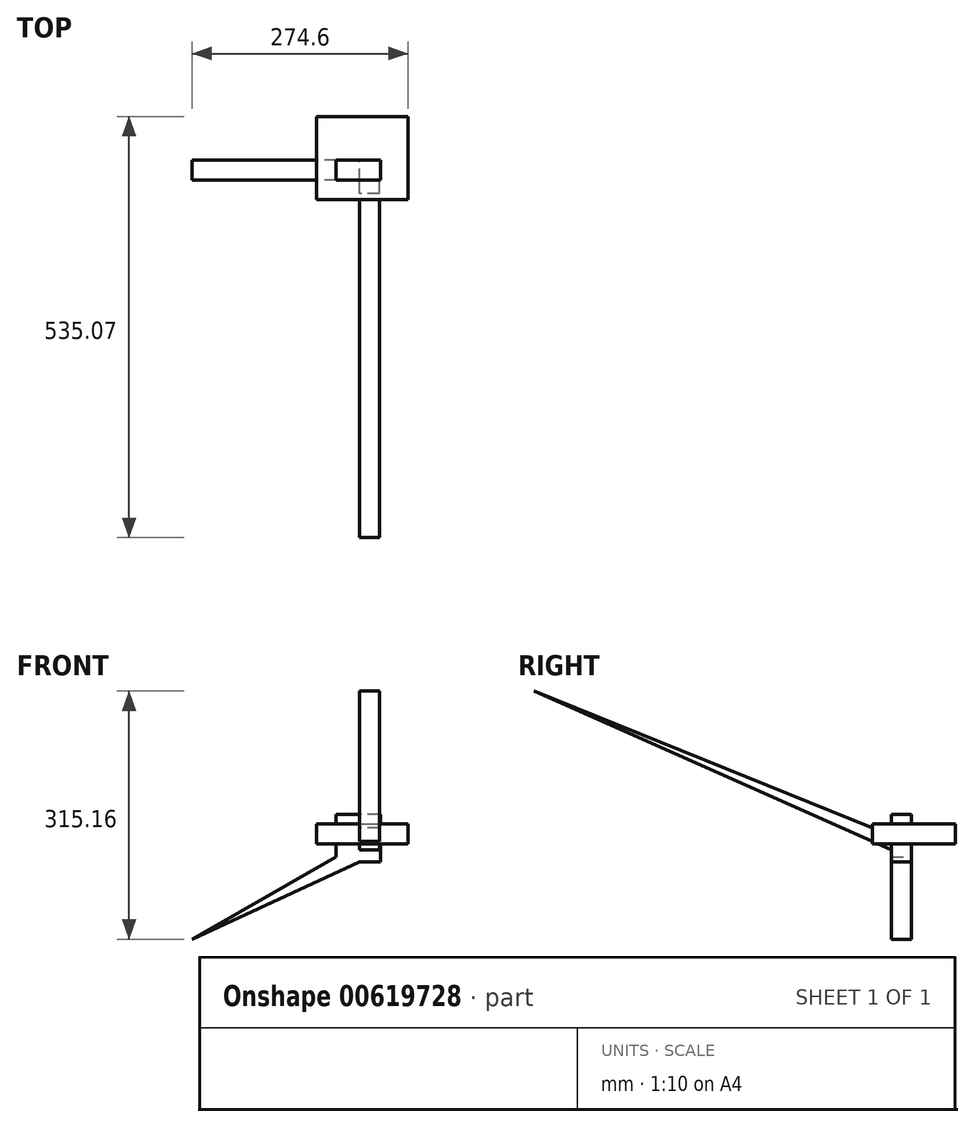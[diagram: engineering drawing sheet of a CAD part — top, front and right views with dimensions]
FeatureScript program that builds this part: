
annotation { "Feature Type Name" : "Feature", "Feature Type Description" : "" }
export const myFeature = defineFeature(function(context is Context, id is Id, definition is map)
    precondition{}
    {
        {
            var Q0;
            Q0=qCreatedBy(makeId("Top.planeOp"),FACE);
            var sketch = newSketch(context, id + "F0", { "sketchPlane" : qUnion([Q0])});
            skLineSegment(sketch, "E0.bottom", {"start": v(0, 0) * mm, "end": v(-54.42, 0) * mm});
            skLineSegment(sketch, "E0.top", {"start": v(0, 55.67) * mm, "end": v(-54.42, 55.67) * mm});
            skLineSegment(sketch, "E0.left", {"start": v(0, 0) * mm, "end": v(0, 55.67) * mm});
            skLineSegment(sketch, "E0.right", {"start": v(-54.42, 0) * mm, "end": v(-54.42, 55.67) * mm});
            skLineSegment(sketch, "E1.bottom", {"start": v(0, 0) * mm, "end": v(61.93, 0) * mm});
            skLineSegment(sketch, "E1.top", {"start": v(0, -49.98) * mm, "end": v(61.93, -49.98) * mm});
            skLineSegment(sketch, "E1.left", {"start": v(0, 0) * mm, "end": v(0, -49.98) * mm});
            skLineSegment(sketch, "E1.right", {"start": v(61.93, 0) * mm, "end": v(61.93, -49.98) * mm});
            skLineSegment(sketch, "E2.top", {"start": v(0, -49.98) * mm, "end": v(-54.42, -49.98) * mm});
            skLineSegment(sketch, "E2.right", {"start": v(-54.42, 0) * mm, "end": v(-54.42, -49.98) * mm});
            skLineSegment(sketch, "E3.top", {"start": v(0, 55.67) * mm, "end": v(61.93, 55.67) * mm});
            skLineSegment(sketch, "E3.right", {"start": v(61.93, 0) * mm, "end": v(61.93, 55.67) * mm});
            skSolve(sketch);
        }
        {
            var Q0;
            Q0=makeQuery(id+"F0.imprint","IMPRINT",FACE,{"disambiguationData":[TD([[makeQuery(id+"F0.imprint","IMPRINT",EDGE,{"derivedFrom":sQuery(id+"F0.wireOp",EDGE,"E1.bottom")}),1.0]])]});
            var Q1;
            Q1=makeQuery(id+"F0.imprint","IMPRINT",FACE,{"disambiguationData":[TD([[makeQuery(id+"F0.imprint","IMPRINT",EDGE,{"derivedFrom":sQuery(id+"F0.wireOp",EDGE,"E1.top")}),1.0]])]});
            var Q2;
            Q2=makeQuery(id+"F0.imprint","IMPRINT",FACE,{"disambiguationData":[TD([[makeQuery(id+"F0.imprint","IMPRINT",EDGE,{"derivedFrom":sQuery(id+"F0.wireOp",EDGE,"E0.bottom")}),1.0]])]});
            var Q3;
            Q3=makeQuery(id+"F0.imprint","IMPRINT",FACE,{"disambiguationData":[TD([[makeQuery(id+"F0.imprint","IMPRINT",EDGE,{"derivedFrom":sQuery(id+"F0.wireOp",EDGE,"E0.top")}),1.0]])]});
            extrude(context, id + "F1", {"entities" : qUnion([Q0, Q1, Q2, Q3]), "depth" : 25.4 * mm, "offsetDistance" : 25.4 * mm});
        }
        {
            var Q0;
            Q0=qCreatedBy(makeId("Front.planeOp"),FACE);
            var sketch = newSketch(context, id + "F2", { "sketchPlane" : qUnion([Q0])});
            skLineSegment(sketch, "E4.bottom", {"start": v(0, 8.65) * mm, "end": v(-29.63, 8.65) * mm});
            skLineSegment(sketch, "E4.top", {"start": v(0, 37.64) * mm, "end": v(-29.63, 37.64) * mm});
            skLineSegment(sketch, "E4.left", {"start": v(0, 8.65) * mm, "end": v(0, 37.64) * mm});
            skLineSegment(sketch, "E4.right", {"start": v(-29.63, 8.65) * mm, "end": v(-29.63, 37.64) * mm});
            skPoint(sketch, "E5.oppositeSnap0", {"position": v(-14.82, 37.64) * mm});
            skLineSegment(sketch, "E5.bottom", {"start": v(0, 8.65) * mm, "end": v(27.02, 8.65) * mm});
            skLineSegment(sketch, "E5.top", {"start": v(0, 37.64) * mm, "end": v(27.02, 37.64) * mm});
            skLineSegment(sketch, "E5.right", {"start": v(27.02, 8.65) * mm, "end": v(27.02, 37.64) * mm});
            skLineSegment(sketch, "E6.top", {"start": v(0, -22.9) * mm, "end": v(27.02, -22.9) * mm});
            skLineSegment(sketch, "E6.left", {"start": v(0, 8.65) * mm, "end": v(0, -22.9) * mm});
            skLineSegment(sketch, "E6.right", {"start": v(27.02, 8.65) * mm, "end": v(27.02, -22.9) * mm});
            skPoint(sketch, "E7.oppositeSnap0", {"position": v(13.5, -22.9) * mm});
            skLineSegment(sketch, "E7.top", {"start": v(0, -22.9) * mm, "end": v(-29.63, -22.9) * mm});
            skLineSegment(sketch, "E7.right", {"start": v(-29.63, 8.65) * mm, "end": v(-29.63, -22.9) * mm});
            skLineSegment(sketch, "E8", {"start": v(0, 0) * mm, "end": v(-212.67, -121.05) * mm});
            skLineSegment(sketch, "E9", {"start": v(-212.67, -121.05) * mm, "end": v(0, -22.9) * mm});
            skSolve(sketch);
        }
        {
            var Q0;
            Q0 = qSketchRegion(id + "F2", true);
            extrude(context, id + "F3", {"entities" : qUnion([Q0]), "operationType" : NewBodyOperationType.ADD, "depth" : 25.4 * mm, "offsetDistance" : 25.4 * mm});
        }
        {
            var Q0;
            Q0=qCreatedBy(makeId("Right.planeOp"),FACE);
            var sketch = newSketch(context, id + "F4", { "sketchPlane" : qUnion([Q0])});
            skLineSegment(sketch, "E10", {"start": v(0, 0) * mm, "end": v(-479.4, 194.11) * mm});
            skLineSegment(sketch, "E11", {"start": v(-479.4, 194.11) * mm, "end": v(0, -18.91) * mm});
            skLineSegment(sketch, "E12", {"start": v(0, -18.91) * mm, "end": v(0, 0) * mm});
            skSolve(sketch);
        }
        {
            var Q0;
            Q0 = qSketchRegion(id + "F4", true);
            extrude(context, id + "F5", {"entities" : qUnion([Q0]), "operationType" : NewBodyOperationType.ADD, "depth" : 25.4 * mm, "offsetDistance" : 25.4 * mm});
        }
    });
